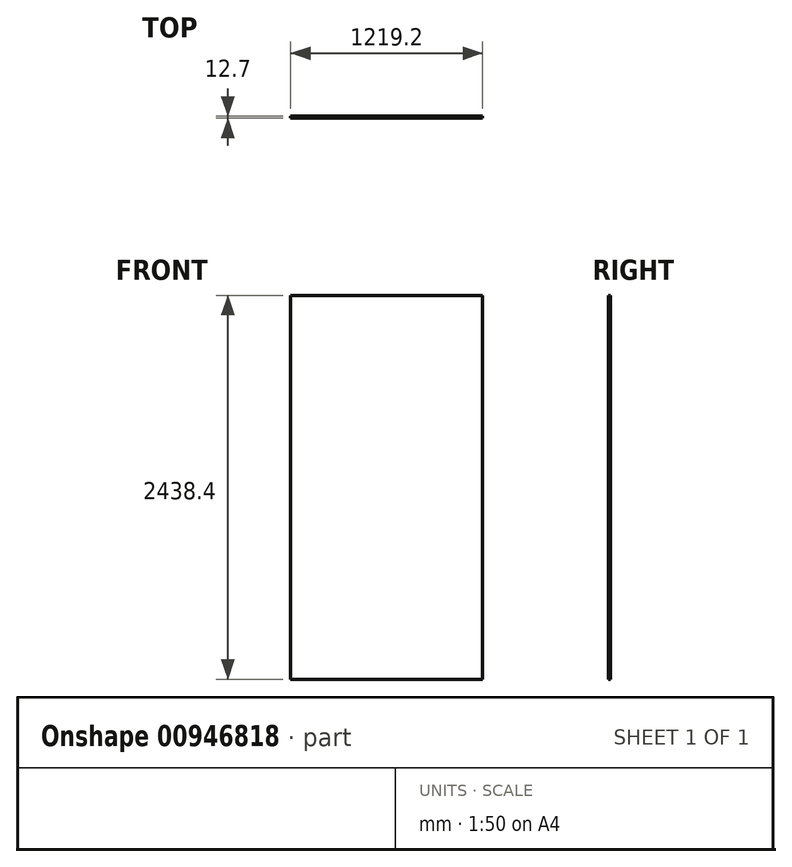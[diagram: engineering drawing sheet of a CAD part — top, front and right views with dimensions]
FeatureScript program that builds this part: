
annotation { "Feature Type Name" : "Feature", "Feature Type Description" : "" }
export const myFeature = defineFeature(function(context is Context, id is Id, definition is map)
    precondition{}
    {
        {
            var Q0;
            Q0=qCreatedBy(makeId("Front.planeOp"),FACE);
            var sketch = newSketch(context, id + "F0", { "sketchPlane" : qUnion([Q0])});
            skLineSegment(sketch, "E0.bottom", {"start": v(0, 0) * mm, "end": v(1219.2, 0) * mm});
            skLineSegment(sketch, "E0.top", {"start": v(0, 2438.4) * mm, "end": v(1219.2, 2438.4) * mm});
            skLineSegment(sketch, "E0.left", {"start": v(0, 0) * mm, "end": v(0, 2438.4) * mm});
            skLineSegment(sketch, "E0.right", {"start": v(1219.2, 0) * mm, "end": v(1219.2, 2438.4) * mm});
            skSolve(sketch);
        }
        {
            var Q0;
            Q0 = qSketchRegion(id + "F0", true);
            extrude(context, id + "F1", {"entities" : qUnion([Q0]), "depth" : 12.7 * mm, "offsetDistance" : 25.4 * mm});
        }
    });
